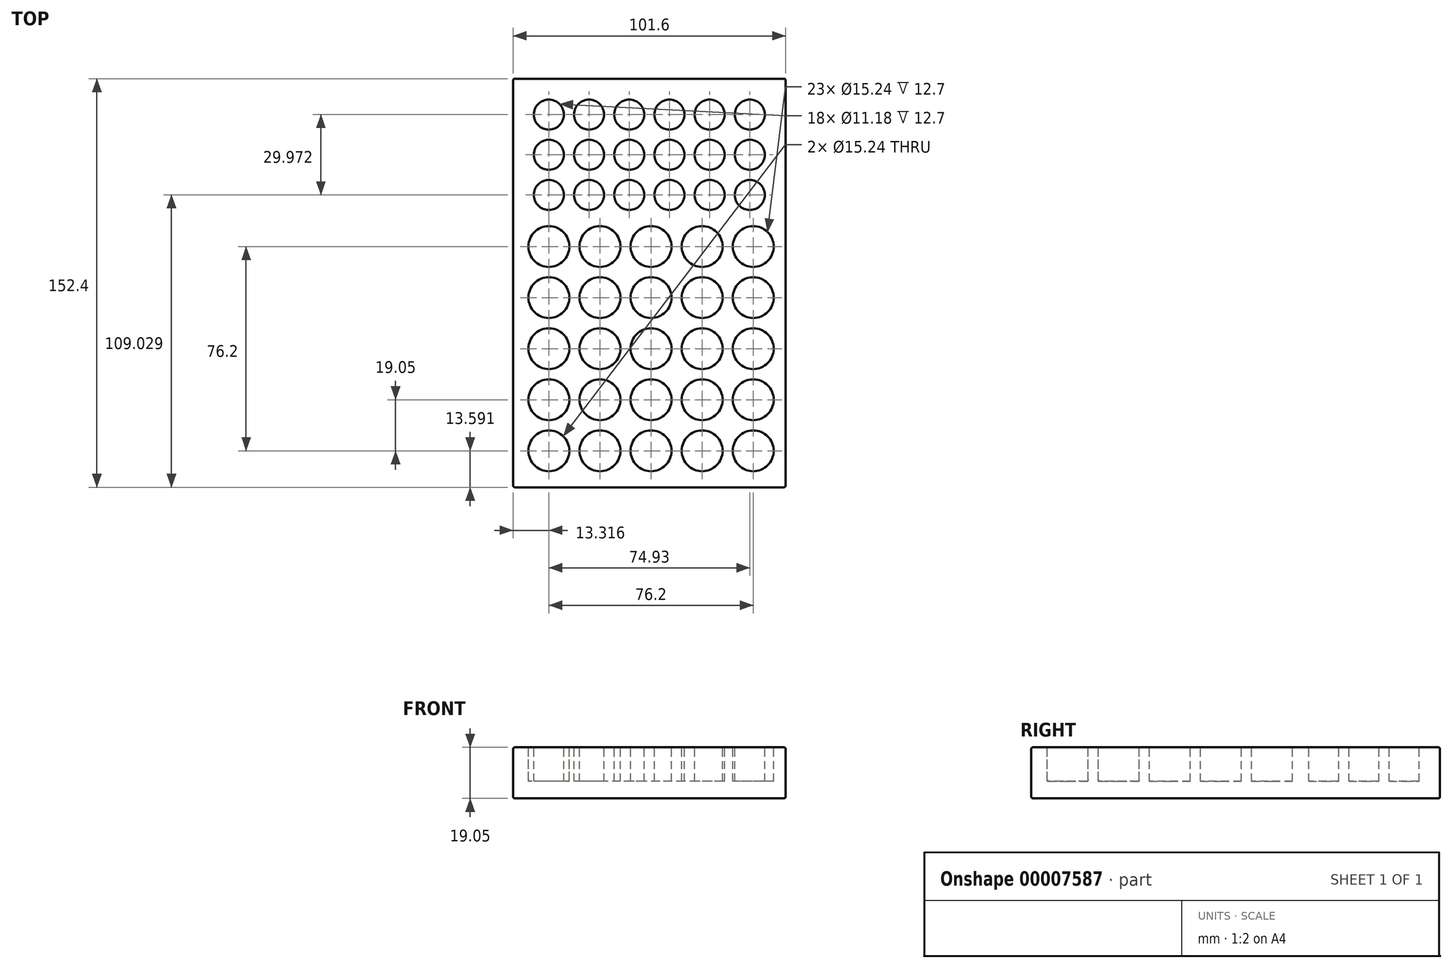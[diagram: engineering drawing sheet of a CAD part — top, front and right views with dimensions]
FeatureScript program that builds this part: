
annotation { "Feature Type Name" : "Feature", "Feature Type Description" : "" }
export const myFeature = defineFeature(function(context is Context, id is Id, definition is map)
    precondition{}
    {
        {
            var Q0;
            Q0=qCreatedBy(makeId("Top.planeOp"),FACE);
            var sketch = newSketch(context, id + "F0", { "sketchPlane" : qUnion([Q0])});
            skLineSegment(sketch, "E0.bottom", {"start": v(0, 0) * mm, "end": v(101.6, 0) * mm});
            skLineSegment(sketch, "E0.top", {"start": v(0, 152.4) * mm, "end": v(101.6, 152.4) * mm});
            skLineSegment(sketch, "E0.left", {"start": v(0, 0) * mm, "end": v(0, 152.4) * mm});
            skLineSegment(sketch, "E0.right", {"start": v(101.6, 0) * mm, "end": v(101.6, 152.4) * mm});
            skSolve(sketch);
        }
        {
            var Q0;
            Q0=makeQuery(id+"F0.imprint","IMPRINT",FACE,{"disambiguationData":[TD([[makeQuery(id+"F0.imprint","IMPRINT",EDGE,{"derivedFrom":sQuery(id+"F0.wireOp",EDGE,"E0.bottom")}),1.0]])]});
            extrude(context, id + "F1", {"entities" : qUnion([Q0]), "depth" : 19.05 * mm});
        }
        {
            var Q0;
            Q0=makeQuery(id+"F1.opExtrude","CAP_FACE",FACE,{"disambiguationData":[OSD([sQuery(id+"F0.wireOp",EDGE,"E0.bottom"),sQuery(id+"F0.wireOp",EDGE,"E0.top"),sQuery(id+"F0.wireOp",EDGE,"E0.left"),sQuery(id+"F0.wireOp",EDGE,"E0.right")])],"isStart":false});
            var sketch = newSketch(context, id + "F2", { "sketchPlane" : qUnion([Q0])});
            skCircle(sketch, "E1", {"center": v(13.32, 13.6) * mm, "radius": 7.62 * mm});
            skCircle(sketch, "E2.0.1.0", {"center": v(13.32, 32.64) * mm, "radius": 7.62 * mm});
            skCircle(sketch, "E2.0.2.0", {"center": v(13.32, 51.7) * mm, "radius": 7.62 * mm});
            skCircle(sketch, "E2.0.3.0", {"center": v(13.32, 70.74) * mm, "radius": 7.62 * mm});
            skCircle(sketch, "E2.1.0.0", {"center": v(32.37, 13.6) * mm, "radius": 7.62 * mm});
            skCircle(sketch, "E2.1.1.0", {"center": v(32.37, 32.64) * mm, "radius": 7.62 * mm});
            skCircle(sketch, "E2.1.2.0", {"center": v(32.37, 51.7) * mm, "radius": 7.62 * mm});
            skCircle(sketch, "E2.1.3.0", {"center": v(32.37, 70.74) * mm, "radius": 7.62 * mm});
            skCircle(sketch, "E2.2.0.0", {"center": v(51.42, 13.6) * mm, "radius": 7.62 * mm});
            skCircle(sketch, "E2.2.1.0", {"center": v(51.42, 32.64) * mm, "radius": 7.62 * mm});
            skCircle(sketch, "E2.2.2.0", {"center": v(51.42, 51.7) * mm, "radius": 7.62 * mm});
            skCircle(sketch, "E2.2.3.0", {"center": v(51.42, 70.74) * mm, "radius": 7.62 * mm});
            skCircle(sketch, "E2.3.0.0", {"center": v(70.47, 13.6) * mm, "radius": 7.62 * mm});
            skCircle(sketch, "E2.3.1.0", {"center": v(70.47, 32.64) * mm, "radius": 7.62 * mm});
            skCircle(sketch, "E2.3.2.0", {"center": v(70.47, 51.7) * mm, "radius": 7.62 * mm});
            skCircle(sketch, "E2.3.3.0", {"center": v(70.47, 70.74) * mm, "radius": 7.62 * mm});
            skCircle(sketch, "E2.4.0.0", {"center": v(89.52, 13.6) * mm, "radius": 7.62 * mm});
            skCircle(sketch, "E2.4.1.0", {"center": v(89.52, 32.64) * mm, "radius": 7.62 * mm});
            skCircle(sketch, "E2.4.2.0", {"center": v(89.52, 51.7) * mm, "radius": 7.62 * mm});
            skCircle(sketch, "E2.4.3.0", {"center": v(89.52, 70.74) * mm, "radius": 7.62 * mm});
            skLineSegment(sketch, "E2.direction1", {"start": v(13.32, 13.6) * mm, "end": v(32.37, 13.6) * mm, "construction": true});
            skLineSegment(sketch, "E2.direction2", {"start": v(13.32, 13.6) * mm, "end": v(13.32, 32.64) * mm, "construction": true});
            skCircle(sketch, "E3.0.0.4", {"center": v(13.32, 89.8) * mm, "radius": 7.62 * mm});
            skCircle(sketch, "E3.0.1.4", {"center": v(32.37, 89.8) * mm, "radius": 7.62 * mm});
            skCircle(sketch, "E3.0.2.4", {"center": v(51.42, 89.8) * mm, "radius": 7.62 * mm});
            skCircle(sketch, "E3.0.3.4", {"center": v(70.47, 89.8) * mm, "radius": 7.62 * mm});
            skCircle(sketch, "E3.0.4.4", {"center": v(89.52, 89.8) * mm, "radius": 7.62 * mm});
            skSolve(sketch);
        }
        {
            var Q0;
            Q0=makeQuery(id+"F2.imprint","IMPRINT",FACE,{"disambiguationData":[TD([[makeQuery(id+"F2.imprint","IMPRINT",EDGE,{"derivedFrom":sQuery(id+"F2.wireOp",EDGE,"E1")}),-1.0]])]});
            var sketch = newSketch(context, id + "F3", { "sketchPlane" : qUnion([Q0])});
            skCircle(sketch, "E4", {"center": v(13.32, 109.03) * mm, "radius": 5.59 * mm});
            skCircle(sketch, "E5.0.1.0", {"center": v(13.32, 124.02) * mm, "radius": 5.59 * mm});
            skCircle(sketch, "E5.0.2.0", {"center": v(13.32, 139) * mm, "radius": 5.59 * mm});
            skCircle(sketch, "E5.1.0.0", {"center": v(28.3, 109.03) * mm, "radius": 5.59 * mm});
            skCircle(sketch, "E5.1.1.0", {"center": v(28.3, 124.02) * mm, "radius": 5.59 * mm});
            skCircle(sketch, "E5.1.2.0", {"center": v(28.3, 139) * mm, "radius": 5.59 * mm});
            skCircle(sketch, "E5.2.0.0", {"center": v(43.29, 109.03) * mm, "radius": 5.59 * mm});
            skCircle(sketch, "E5.2.1.0", {"center": v(43.29, 124.02) * mm, "radius": 5.59 * mm});
            skCircle(sketch, "E5.2.2.0", {"center": v(43.29, 139) * mm, "radius": 5.59 * mm});
            skCircle(sketch, "E5.3.0.0", {"center": v(58.27, 109.03) * mm, "radius": 5.59 * mm});
            skCircle(sketch, "E5.3.1.0", {"center": v(58.27, 124.02) * mm, "radius": 5.59 * mm});
            skCircle(sketch, "E5.3.2.0", {"center": v(58.27, 139) * mm, "radius": 5.59 * mm});
            skCircle(sketch, "E5.4.0.0", {"center": v(73.26, 109.03) * mm, "radius": 5.59 * mm});
            skCircle(sketch, "E5.4.1.0", {"center": v(73.26, 124.02) * mm, "radius": 5.59 * mm});
            skCircle(sketch, "E5.4.2.0", {"center": v(73.26, 139) * mm, "radius": 5.59 * mm});
            skCircle(sketch, "E5.5.0.0", {"center": v(88.25, 109.03) * mm, "radius": 5.59 * mm});
            skCircle(sketch, "E5.5.1.0", {"center": v(88.25, 124.02) * mm, "radius": 5.59 * mm});
            skCircle(sketch, "E5.5.2.0", {"center": v(88.25, 139) * mm, "radius": 5.59 * mm});
            skLineSegment(sketch, "E5.direction1", {"start": v(13.32, 109.03) * mm, "end": v(28.3, 109.03) * mm, "construction": true});
            skLineSegment(sketch, "E5.direction2", {"start": v(13.32, 109.03) * mm, "end": v(13.32, 124.02) * mm, "construction": true});
            skSolve(sketch);
        }
        {
            var Q0;
            Q0 = qSketchRegion(id + "F3", true);
            var Q1;
            Q1 = qSketchRegion(id + "F2", true);
            extrude(context, id + "F4", {"entities" : qUnion([Q0, Q1]), "operationType" : NewBodyOperationType.REMOVE, "oppositeDirection" : true, "depth" : 12.7 * mm});
        }
        {
            var Q0;
            Q0=makeQuery(id+"F4.boolean.opBoolean","COPY",EDGE,{"derivedFrom":makeQuery(id+"F4.opExtrude","CAP_EDGE",EDGE,{"disambiguationData":[OSD([sQuery(id+"F3.wireOp",EDGE,"E5.0.2.0")])],"isStart":true})});
            var Q1;
            Q1=makeQuery(id+"F4.boolean.opBoolean","COPY",EDGE,{"derivedFrom":makeQuery(id+"F4.opExtrude","CAP_EDGE",EDGE,{"disambiguationData":[OSD([sQuery(id+"F3.wireOp",EDGE,"E5.1.2.0")])],"isStart":true})});
            var Q2;
            Q2=makeQuery(id+"F4.boolean.opBoolean","COPY",EDGE,{"derivedFrom":makeQuery(id+"F4.opExtrude","CAP_EDGE",EDGE,{"disambiguationData":[OSD([sQuery(id+"F3.wireOp",EDGE,"E5.2.2.0")])],"isStart":true})});
            var Q3;
            Q3=makeQuery(id+"F4.boolean.opBoolean","COPY",EDGE,{"derivedFrom":makeQuery(id+"F4.opExtrude","CAP_EDGE",EDGE,{"disambiguationData":[OSD([sQuery(id+"F3.wireOp",EDGE,"E5.3.2.0")])],"isStart":true})});
            var Q4;
            Q4=makeQuery(id+"F4.boolean.opBoolean","COPY",EDGE,{"derivedFrom":makeQuery(id+"F4.opExtrude","CAP_EDGE",EDGE,{"disambiguationData":[OSD([sQuery(id+"F3.wireOp",EDGE,"E5.4.2.0")])],"isStart":true})});
            var Q5;
            Q5=makeQuery(id+"F4.boolean.opBoolean","COPY",EDGE,{"derivedFrom":makeQuery(id+"F4.opExtrude","CAP_EDGE",EDGE,{"disambiguationData":[OSD([sQuery(id+"F3.wireOp",EDGE,"E5.5.2.0")])],"isStart":true})});
            var Q6;
            Q6=makeQuery(id+"F4.boolean.opBoolean","COPY",EDGE,{"derivedFrom":makeQuery(id+"F4.opExtrude","CAP_EDGE",EDGE,{"disambiguationData":[OSD([sQuery(id+"F3.wireOp",EDGE,"E5.5.1.0")])],"isStart":true})});
            var Q7;
            Q7=makeQuery(id+"F4.boolean.opBoolean","COPY",EDGE,{"derivedFrom":makeQuery(id+"F4.opExtrude","CAP_EDGE",EDGE,{"disambiguationData":[OSD([sQuery(id+"F3.wireOp",EDGE,"E5.4.1.0")])],"isStart":true})});
            var Q8;
            Q8=makeQuery(id+"F4.boolean.opBoolean","COPY",EDGE,{"derivedFrom":makeQuery(id+"F4.opExtrude","CAP_EDGE",EDGE,{"disambiguationData":[OSD([sQuery(id+"F3.wireOp",EDGE,"E5.3.1.0")])],"isStart":true})});
            var Q9;
            Q9=makeQuery(id+"F4.boolean.opBoolean","COPY",EDGE,{"derivedFrom":makeQuery(id+"F4.opExtrude","CAP_EDGE",EDGE,{"disambiguationData":[OSD([sQuery(id+"F3.wireOp",EDGE,"E5.2.1.0")])],"isStart":true})});
            var Q10;
            Q10=makeQuery(id+"F4.boolean.opBoolean","COPY",EDGE,{"derivedFrom":makeQuery(id+"F4.opExtrude","CAP_EDGE",EDGE,{"disambiguationData":[OSD([sQuery(id+"F3.wireOp",EDGE,"E5.1.1.0")])],"isStart":true})});
            var Q11;
            Q11=makeQuery(id+"F4.boolean.opBoolean","COPY",EDGE,{"derivedFrom":makeQuery(id+"F4.opExtrude","CAP_EDGE",EDGE,{"disambiguationData":[OSD([sQuery(id+"F3.wireOp",EDGE,"E5.0.1.0")])],"isStart":true})});
            var Q12;
            Q12=makeQuery(id+"F4.boolean.opBoolean","COPY",EDGE,{"derivedFrom":makeQuery(id+"F4.opExtrude","CAP_EDGE",EDGE,{"disambiguationData":[OSD([sQuery(id+"F3.wireOp",EDGE,"E4")])],"isStart":true})});
            var Q13;
            Q13=makeQuery(id+"F4.boolean.opBoolean","COPY",EDGE,{"derivedFrom":makeQuery(id+"F4.opExtrude","CAP_EDGE",EDGE,{"disambiguationData":[OSD([sQuery(id+"F3.wireOp",EDGE,"E5.1.0.0")])],"isStart":true})});
            var Q14;
            Q14=makeQuery(id+"F4.boolean.opBoolean","COPY",EDGE,{"derivedFrom":makeQuery(id+"F4.opExtrude","CAP_EDGE",EDGE,{"disambiguationData":[OSD([sQuery(id+"F3.wireOp",EDGE,"E5.2.0.0")])],"isStart":true})});
            var Q15;
            Q15=makeQuery(id+"F4.boolean.opBoolean","COPY",EDGE,{"derivedFrom":makeQuery(id+"F4.opExtrude","CAP_EDGE",EDGE,{"disambiguationData":[OSD([sQuery(id+"F3.wireOp",EDGE,"E5.3.0.0")])],"isStart":true})});
            var Q16;
            Q16=makeQuery(id+"F4.boolean.opBoolean","COPY",EDGE,{"derivedFrom":makeQuery(id+"F4.opExtrude","CAP_EDGE",EDGE,{"disambiguationData":[OSD([sQuery(id+"F3.wireOp",EDGE,"E5.4.0.0")])],"isStart":true})});
            var Q17;
            Q17=makeQuery(id+"F4.boolean.opBoolean","COPY",EDGE,{"derivedFrom":makeQuery(id+"F4.opExtrude","CAP_EDGE",EDGE,{"disambiguationData":[OSD([sQuery(id+"F3.wireOp",EDGE,"E5.5.0.0")])],"isStart":true})});
            var Q18;
            Q18=makeQuery(id+"F4.boolean.opBoolean","COPY",EDGE,{"derivedFrom":makeQuery(id+"F4.opExtrude","CAP_EDGE",EDGE,{"disambiguationData":[OSD([sQuery(id+"F2.wireOp",EDGE,"E3.0.4.4")])],"isStart":true})});
            var Q19;
            Q19=makeQuery(id+"F4.boolean.opBoolean","COPY",EDGE,{"derivedFrom":makeQuery(id+"F4.opExtrude","CAP_EDGE",EDGE,{"disambiguationData":[OSD([sQuery(id+"F2.wireOp",EDGE,"E3.0.3.4")])],"isStart":true})});
            var Q20;
            Q20=makeQuery(id+"F4.boolean.opBoolean","COPY",EDGE,{"derivedFrom":makeQuery(id+"F4.opExtrude","CAP_EDGE",EDGE,{"disambiguationData":[OSD([sQuery(id+"F2.wireOp",EDGE,"E3.0.2.4")])],"isStart":true})});
            var Q21;
            Q21=makeQuery(id+"F4.boolean.opBoolean","COPY",EDGE,{"derivedFrom":makeQuery(id+"F4.opExtrude","CAP_EDGE",EDGE,{"disambiguationData":[OSD([sQuery(id+"F2.wireOp",EDGE,"E3.0.1.4")])],"isStart":true})});
            var Q22;
            Q22=makeQuery(id+"F4.boolean.opBoolean","COPY",EDGE,{"derivedFrom":makeQuery(id+"F4.opExtrude","CAP_EDGE",EDGE,{"disambiguationData":[OSD([sQuery(id+"F2.wireOp",EDGE,"E2.0.3.0")])],"isStart":true})});
            var Q23;
            Q23=makeQuery(id+"F4.boolean.opBoolean","COPY",EDGE,{"derivedFrom":makeQuery(id+"F4.opExtrude","CAP_EDGE",EDGE,{"disambiguationData":[OSD([sQuery(id+"F2.wireOp",EDGE,"E3.0.0.4")])],"isStart":true})});
            var Q24;
            Q24=makeQuery(id+"F4.boolean.opBoolean","COPY",EDGE,{"derivedFrom":makeQuery(id+"F4.opExtrude","CAP_EDGE",EDGE,{"disambiguationData":[OSD([sQuery(id+"F2.wireOp",EDGE,"E2.1.3.0")])],"isStart":true})});
            var Q25;
            Q25=makeQuery(id+"F4.boolean.opBoolean","COPY",EDGE,{"derivedFrom":makeQuery(id+"F4.opExtrude","CAP_EDGE",EDGE,{"disambiguationData":[OSD([sQuery(id+"F2.wireOp",EDGE,"E2.2.3.0")])],"isStart":true})});
            var Q26;
            Q26=makeQuery(id+"F1.opExtrude","CAP_EDGE",EDGE,{"disambiguationData":[OSD([sQuery(id+"F0.wireOp",EDGE,"E0.right")])],"isStart":false});
            var Q27;
            Q27=makeQuery(id+"F1.opExtrude","CAP_EDGE",EDGE,{"disambiguationData":[OSD([sQuery(id+"F0.wireOp",EDGE,"E0.bottom")])],"isStart":false});
            var Q28;
            Q28=makeQuery(id+"F1.opExtrude","CAP_EDGE",EDGE,{"disambiguationData":[OSD([sQuery(id+"F0.wireOp",EDGE,"E0.left")])],"isStart":false});
            var Q29;
            Q29=makeQuery(id+"F1.opExtrude","CAP_EDGE",EDGE,{"disambiguationData":[OSD([sQuery(id+"F0.wireOp",EDGE,"E0.top")])],"isStart":false});
            var Q30;
            Q30=makeQuery(id+"F1.opExtrude","SWEPT_EDGE",EDGE,{"disambiguationData":[OSD([sQuery(id+"F0.wireOp",EDGE,"E0.top"),sQuery(id+"F0.wireOp",EDGE,"E0.right")])]});
            var Q31;
            Q31=makeQuery(id+"F1.opExtrude","CAP_EDGE",EDGE,{"disambiguationData":[OSD([sQuery(id+"F0.wireOp",EDGE,"E0.right")])],"isStart":true});
            var Q32;
            Q32=makeQuery(id+"F1.opExtrude","SWEPT_EDGE",EDGE,{"disambiguationData":[OSD([sQuery(id+"F0.wireOp",EDGE,"E0.bottom"),sQuery(id+"F0.wireOp",EDGE,"E0.right")])]});
            var Q33;
            Q33=makeQuery(id+"F1.opExtrude","CAP_EDGE",EDGE,{"disambiguationData":[OSD([sQuery(id+"F0.wireOp",EDGE,"E0.bottom")])],"isStart":true});
            var Q34;
            Q34=makeQuery(id+"F1.opExtrude","SWEPT_EDGE",EDGE,{"disambiguationData":[OSD([sQuery(id+"F0.wireOp",EDGE,"E0.bottom"),sQuery(id+"F0.wireOp",EDGE,"E0.left")])]});
            var Q35;
            Q35=makeQuery(id+"F1.opExtrude","SWEPT_FACE",FACE,{"disambiguationData":[OSD([sQuery(id+"F0.wireOp",EDGE,"E0.top")])]});
            var Q36;
            Q36=makeQuery(id+"F1.opExtrude","CAP_EDGE",EDGE,{"disambiguationData":[OSD([sQuery(id+"F0.wireOp",EDGE,"E0.top")])],"isStart":true});
            var Q37;
            Q37=makeQuery(id+"F1.opExtrude","SWEPT_EDGE",EDGE,{"disambiguationData":[OSD([sQuery(id+"F0.wireOp",EDGE,"E0.top"),sQuery(id+"F0.wireOp",EDGE,"E0.left")])]});
            var Q38;
            Q38=makeQuery(id+"F1.opExtrude","CAP_EDGE",EDGE,{"disambiguationData":[OSD([sQuery(id+"F0.wireOp",EDGE,"E0.left")])],"isStart":true});
            var Q39;
            Q39=makeQuery(id+"F4.boolean.opBoolean","COPY",EDGE,{"derivedFrom":makeQuery(id+"F4.opExtrude","CAP_EDGE",EDGE,{"disambiguationData":[OSD([sQuery(id+"F2.wireOp",EDGE,"E2.0.2.0")])],"isStart":true})});
            var Q40;
            Q40=makeQuery(id+"F4.boolean.opBoolean","COPY",EDGE,{"derivedFrom":makeQuery(id+"F4.opExtrude","CAP_EDGE",EDGE,{"disambiguationData":[OSD([sQuery(id+"F2.wireOp",EDGE,"E2.0.1.0")])],"isStart":false})});
            var Q41;
            Q41=makeQuery(id+"F4.boolean.opBoolean","COPY",EDGE,{"derivedFrom":makeQuery(id+"F4.opExtrude","CAP_EDGE",EDGE,{"disambiguationData":[OSD([sQuery(id+"F2.wireOp",EDGE,"E1")])],"isStart":false})});
            var Q42;
            Q42=makeQuery(id+"F4.boolean.opBoolean","COPY",EDGE,{"derivedFrom":makeQuery(id+"F4.opExtrude","CAP_EDGE",EDGE,{"disambiguationData":[OSD([sQuery(id+"F2.wireOp",EDGE,"E2.1.0.0")])],"isStart":true})});
            var Q43;
            Q43=makeQuery(id+"F4.boolean.opBoolean","COPY",EDGE,{"derivedFrom":makeQuery(id+"F4.opExtrude","CAP_EDGE",EDGE,{"disambiguationData":[OSD([sQuery(id+"F2.wireOp",EDGE,"E2.1.1.0")])],"isStart":true})});
            var Q44;
            Q44=makeQuery(id+"F4.boolean.opBoolean","COPY",EDGE,{"derivedFrom":makeQuery(id+"F4.opExtrude","CAP_EDGE",EDGE,{"disambiguationData":[OSD([sQuery(id+"F2.wireOp",EDGE,"E2.1.2.0")])],"isStart":true})});
            var Q45;
            Q45=makeQuery(id+"F4.boolean.opBoolean","COPY",EDGE,{"derivedFrom":makeQuery(id+"F4.opExtrude","CAP_EDGE",EDGE,{"disambiguationData":[OSD([sQuery(id+"F2.wireOp",EDGE,"E2.2.2.0")])],"isStart":true})});
            var Q46;
            Q46=makeQuery(id+"F4.boolean.opBoolean","COPY",EDGE,{"derivedFrom":makeQuery(id+"F4.opExtrude","CAP_EDGE",EDGE,{"disambiguationData":[OSD([sQuery(id+"F2.wireOp",EDGE,"E2.2.1.0")])],"isStart":true})});
            var Q47;
            Q47=makeQuery(id+"F4.boolean.opBoolean","COPY",EDGE,{"derivedFrom":makeQuery(id+"F4.opExtrude","CAP_EDGE",EDGE,{"disambiguationData":[OSD([sQuery(id+"F2.wireOp",EDGE,"E2.2.0.0")])],"isStart":true})});
            var Q48;
            Q48=makeQuery(id+"F4.boolean.opBoolean","COPY",EDGE,{"derivedFrom":makeQuery(id+"F4.opExtrude","CAP_EDGE",EDGE,{"disambiguationData":[OSD([sQuery(id+"F2.wireOp",EDGE,"E2.3.0.0")])],"isStart":true})});
            var Q49;
            Q49=makeQuery(id+"F4.boolean.opBoolean","COPY",EDGE,{"derivedFrom":makeQuery(id+"F4.opExtrude","CAP_EDGE",EDGE,{"disambiguationData":[OSD([sQuery(id+"F2.wireOp",EDGE,"E2.3.1.0")])],"isStart":true})});
            var Q50;
            Q50=makeQuery(id+"F4.boolean.opBoolean","COPY",EDGE,{"derivedFrom":makeQuery(id+"F4.opExtrude","CAP_EDGE",EDGE,{"disambiguationData":[OSD([sQuery(id+"F2.wireOp",EDGE,"E2.3.2.0")])],"isStart":true})});
            var Q51;
            Q51=makeQuery(id+"F4.boolean.opBoolean","COPY",EDGE,{"derivedFrom":makeQuery(id+"F4.opExtrude","CAP_EDGE",EDGE,{"disambiguationData":[OSD([sQuery(id+"F2.wireOp",EDGE,"E2.3.3.0")])],"isStart":true})});
            var Q52;
            Q52=makeQuery(id+"F4.boolean.opBoolean","COPY",EDGE,{"derivedFrom":makeQuery(id+"F4.opExtrude","CAP_EDGE",EDGE,{"disambiguationData":[OSD([sQuery(id+"F2.wireOp",EDGE,"E2.4.2.0")])],"isStart":true})});
            var Q53;
            Q53=makeQuery(id+"F4.boolean.opBoolean","COPY",EDGE,{"derivedFrom":makeQuery(id+"F4.opExtrude","CAP_EDGE",EDGE,{"disambiguationData":[OSD([sQuery(id+"F2.wireOp",EDGE,"E2.4.3.0")])],"isStart":true})});
            var Q54;
            Q54=makeQuery(id+"F4.boolean.opBoolean","COPY",EDGE,{"derivedFrom":makeQuery(id+"F4.opExtrude","CAP_EDGE",EDGE,{"disambiguationData":[OSD([sQuery(id+"F2.wireOp",EDGE,"E2.4.1.0")])],"isStart":true})});
            var Q55;
            Q55=makeQuery(id+"F4.boolean.opBoolean","COPY",EDGE,{"derivedFrom":makeQuery(id+"F4.opExtrude","CAP_EDGE",EDGE,{"disambiguationData":[OSD([sQuery(id+"F2.wireOp",EDGE,"E2.4.0.0")])],"isStart":true})});
            fillet(context, id + "F5", {"entities" : qUnion([Q0, Q1, Q2, Q3, Q4, Q5, Q6, Q7, Q8, Q9, Q10, Q11, Q12, Q13, Q14, Q15, Q16, Q17, Q18, Q19, Q20, Q21, Q22, Q23, Q24, Q25, Q26, Q27, Q28, Q29, Q30, Q31, Q32, Q33, Q34, Q35, Q36, Q37, Q38, Q39, Q40, Q41, Q42, Q43, Q44, Q45, Q46, Q47, Q48, Q49, Q50, Q51, Q52, Q53, Q54, Q55]), "radius" : 0.64 * mm, "tangentPropagation" : true, "allowEdgeOverflow" : false});
        }
    });
